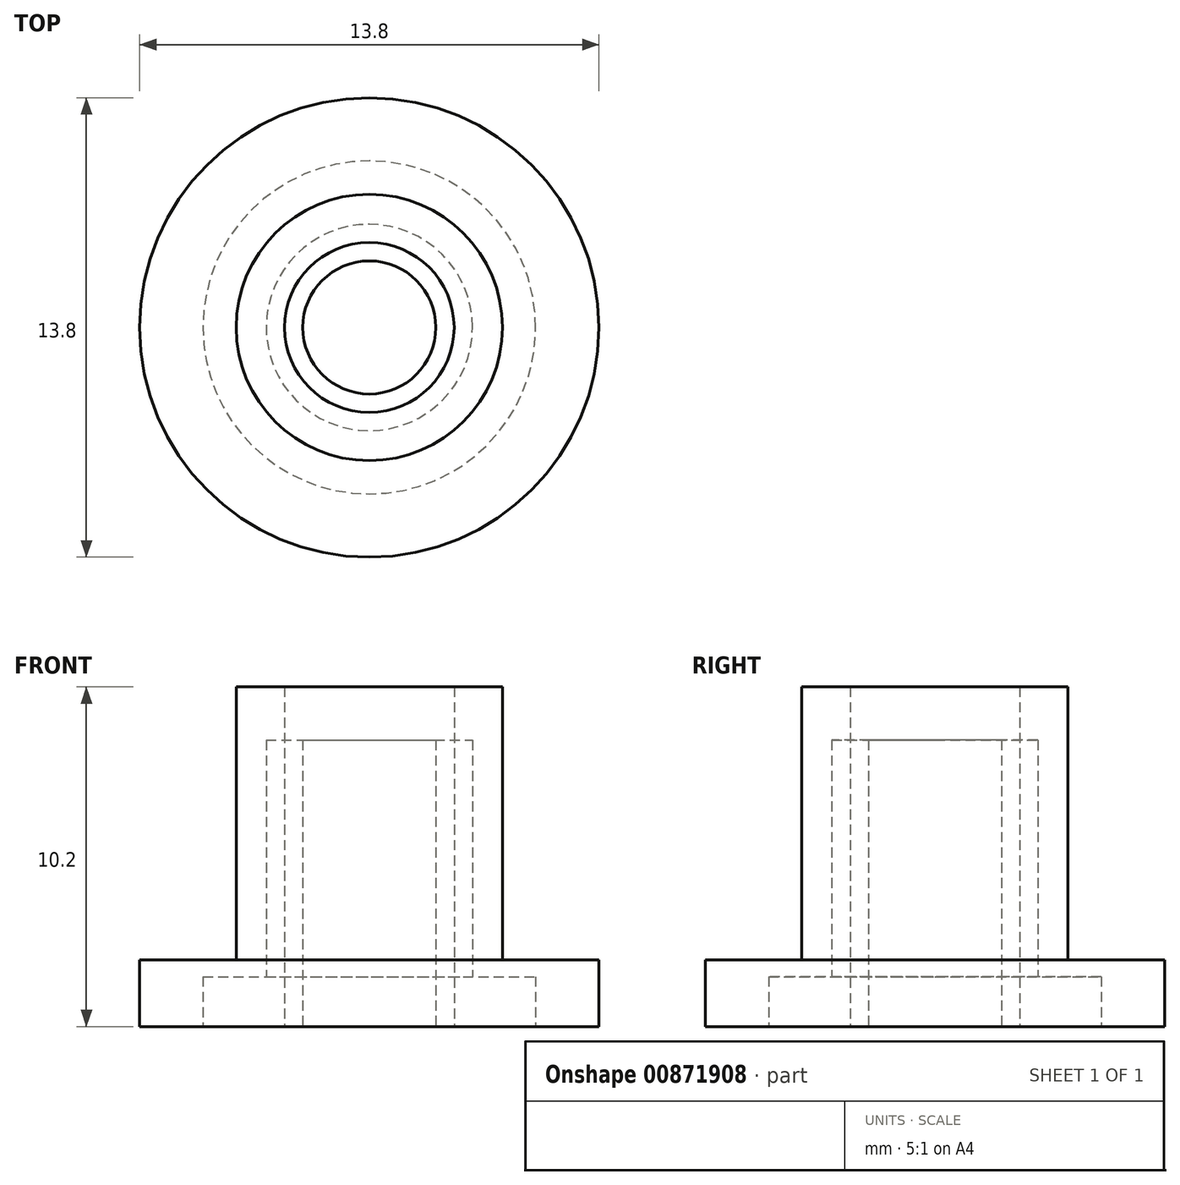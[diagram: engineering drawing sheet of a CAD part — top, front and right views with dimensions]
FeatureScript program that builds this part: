
annotation { "Feature Type Name" : "Feature", "Feature Type Description" : "" }
export const myFeature = defineFeature(function(context is Context, id is Id, definition is map)
    precondition{}
    {
        {
            var Q0;
            Q0=qCreatedBy(makeId("Front.planeOp"),FACE);
            var sketch = newSketch(context, id + "F0", { "sketchPlane" : qUnion([Q0])});
            skLineSegment(sketch, "E0", {"start": v(0, 0) * mm, "end": v(0, 12.5) * mm, "construction": true});
            skLineSegment(sketch, "E1", {"start": v(-2, 0) * mm, "end": v(-2, 8.6) * mm});
            skLineSegment(sketch, "E2", {"start": v(-2, 8.6) * mm, "end": v(-3.1, 8.6) * mm});
            skLineSegment(sketch, "E3", {"start": v(-3.1, 8.6) * mm, "end": v(-3.1, 1.5) * mm});
            skLineSegment(sketch, "E4", {"start": v(-3.1, 1.5) * mm, "end": v(-5, 1.5) * mm});
            skLineSegment(sketch, "E5", {"start": v(-5, 1.5) * mm, "end": v(-5, 0) * mm});
            skLineSegment(sketch, "E6", {"start": v(-5, 0) * mm, "end": v(-2, 0) * mm});
            skSolve(sketch);
        }
        {
            var Q0;
            Q0=makeQuery(id+"F0.imprint","IMPRINT",FACE,{"disambiguationData":[TD([[makeQuery(id+"F0.imprint","IMPRINT",EDGE,{"derivedFrom":sQuery(id+"F0.wireOp",EDGE,"E1")}),1.0]])]});
            var Q1;
            Q1=sQuery(id+"F0.wireOp",EDGE,"E0");
            revolve(context, id + "F1", {"surfaceOperationType" : NewSurfaceOperationType.NEW, "entities" : qUnion([Q0]), "axis" : qUnion([Q1]), "revolveType" : RevolveType.FULL});
        }
        {
            var Q0;
            Q0=qCreatedBy(makeId("Front.planeOp"),FACE);
            var sketch = newSketch(context, id + "F2", { "sketchPlane" : qUnion([Q0])});
            skLineSegment(sketch, "E7", {"start": v(0, 0) * mm, "end": v(0, 9.24) * mm, "construction": true});
            skLineSegment(sketch, "E8", {"start": v(-2.55, 0) * mm, "end": v(-2.55, 10.2) * mm});
            skLineSegment(sketch, "E9", {"start": v(-2.55, 10.2) * mm, "end": v(-4, 10.2) * mm});
            skLineSegment(sketch, "E10", {"start": v(-4, 10.2) * mm, "end": v(-4, 2) * mm});
            skLineSegment(sketch, "E11", {"start": v(-4, 2) * mm, "end": v(-6.9, 2) * mm});
            skLineSegment(sketch, "E12", {"start": v(-6.9, 2) * mm, "end": v(-6.9, 0) * mm});
            skLineSegment(sketch, "E13", {"start": v(-6.9, 0) * mm, "end": v(-2.55, 0) * mm});
            skSolve(sketch);
        }
        {
            var Q0;
            Q0=qSketchRegion(id+"F2",true);
            var Q1;
            Q1=sQuery(id+"F2.wireOp",EDGE,"E7");
            revolve(context, id + "F3", {"surfaceOperationType" : NewSurfaceOperationType.NEW, "entities" : qUnion([Q0]), "axis" : qUnion([Q1]), "revolveType" : RevolveType.FULL});
        }
    });
